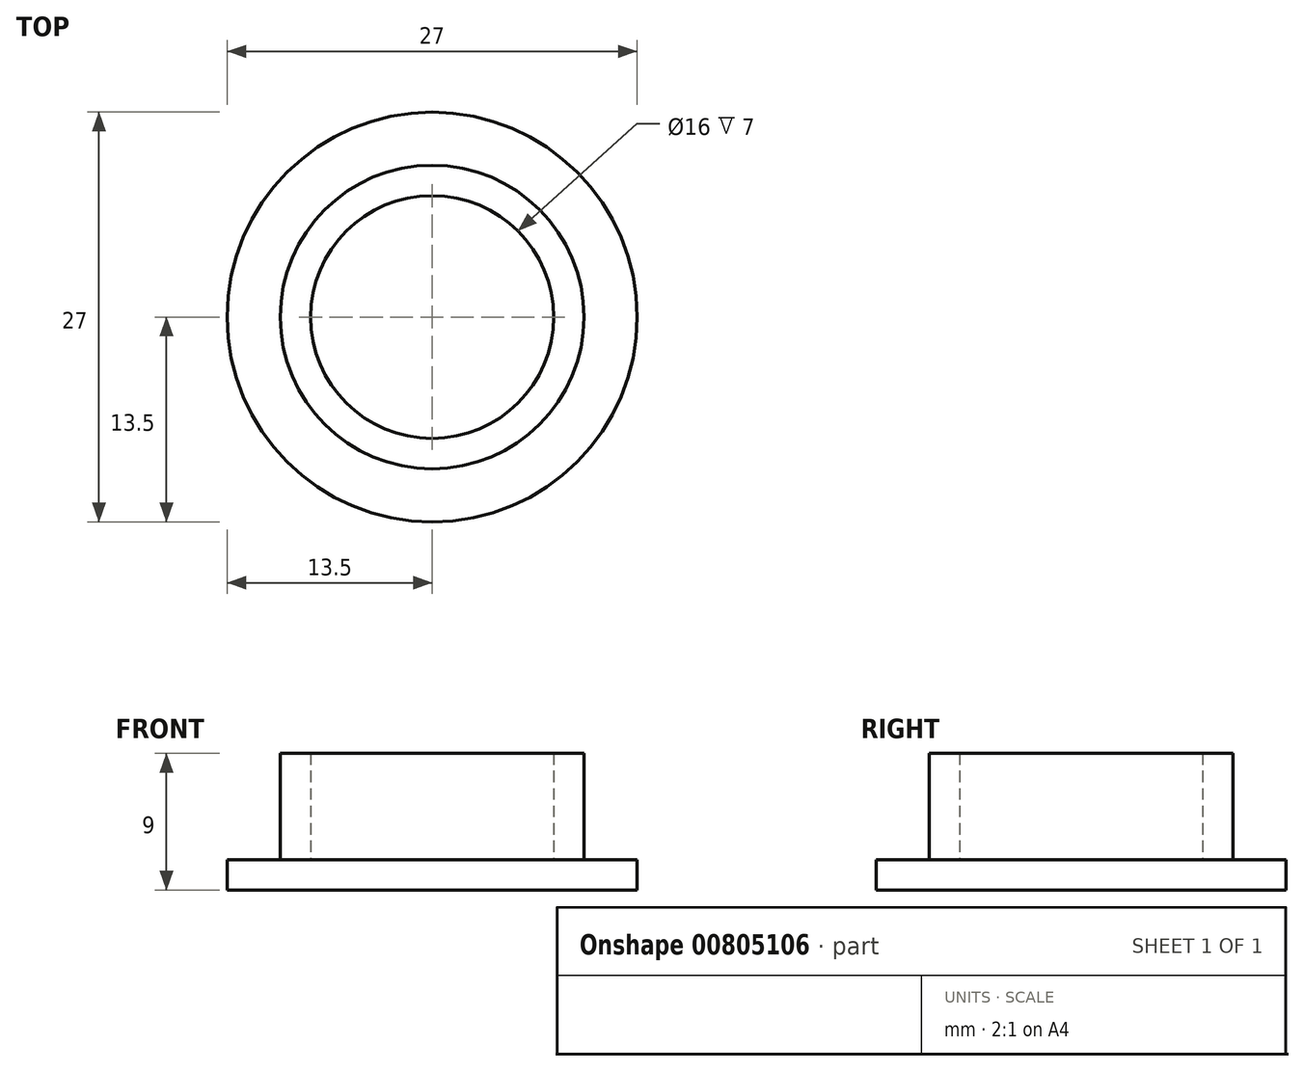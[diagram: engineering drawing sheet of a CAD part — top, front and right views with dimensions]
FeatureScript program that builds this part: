
annotation { "Feature Type Name" : "Feature", "Feature Type Description" : "" }
export const myFeature = defineFeature(function(context is Context, id is Id, definition is map)
    precondition{}
    {
        {
            var Q0;
            Q0=qCreatedBy(makeId("Top.planeOp"),FACE);
            var sketch = newSketch(context, id + "F0", { "sketchPlane" : qUnion([Q0])});
            skCircle(sketch, "E0", {"center": v(0, 0) * mm, "radius": 13.5 * mm});
            skSolve(sketch);
        }
        {
            var Q0;
            Q0=qSketchRegion(id+"F0",true);
            extrude(context, id + "F1", {"entities" : qUnion([Q0]), "depth" : 2 * mm, "offsetDistance" : 25 * mm});
        }
        {
            var Q0;
            Q0=makeQuery(id+"F1.opExtrude","CAP_FACE",FACE,{"disambiguationData":[OSD([sQuery(id+"F0.wireOp",EDGE,"E0")])],"isStart":false});
            var sketch = newSketch(context, id + "F2", { "sketchPlane" : qUnion([Q0])});
            skCircle(sketch, "E1", {"center": v(0, 0) * mm, "radius": 10 * mm});
            skCircle(sketch, "E2", {"center": v(0, 0) * mm, "radius": 8 * mm});
            skSolve(sketch);
        }
        {
            var Q0;
            Q0=makeQuery(id+"F2.imprint","IMPRINT",FACE,{"disambiguationData":[TD([[makeQuery(id+"F2.imprint","IMPRINT",EDGE,{"derivedFrom":sQuery(id+"F2.wireOp",EDGE,"E1")}),1.0]])]});
            extrude(context, id + "F3", {"entities" : qUnion([Q0]), "operationType" : NewBodyOperationType.ADD, "depth" : 7 * mm, "offsetDistance" : 25 * mm});
        }
    });
